# Revit family: RS500.80.x.245
name_source: partatom
category: Allgemeines Modell
units: mm (PartAtom-declared; Revit-internal decimal feet)

## family parameters
Arbeitsebenenbasiert = Nein
Beim Laden mit Abzugskörper schneiden = Nein
Bemaßung runder Anschluss = Durchmesser verwenden
Gemeinsam genutzt = Nein
Immer vertikal = Ja
Kann Basisbauteil für Bewehrung sein = Nein
Raumberechnungspunkt = Nein
Teiletyp = Normal

## types (1)
- DN80
    Anschlusswert DU L/s = 0
    Baugruppenkennzeichen = D2030300
    Hersteller = Resitec
    RS_AVol-H = 200 mm  [stored 0.656168 ft]
    RS_AVol-L = 129 mm  [stored 0.423228 ft]
    RS_AVol-T = 129 mm  [stored 0.423228 ft]
    RS_DN1 = 80 mm  [stored 0.262467 ft]
    RS_DN1d = 88 mm  [stored 0.288714 ft]
    RS_DN2 = 180 mm  [stored 0.590551 ft]
    RS_DVol-L = 200 mm  [stored 0.656168 ft]
    RS_DVol-T = 200 mm  [stored 0.656168 ft]
    RS_Klbl = 2 mm  [stored 0.00656168 ft]
    RS_Manufacture = Resitec
    RS_URL = https://resitec.ch
    RS_dia001 = 245 mm  [stored 0.803806 ft]
    RS_dia002 = 130 mm  [stored 0.426509 ft]
    RS_dim001 = 23 mm  [stored 0.0754593 ft]
    RS_dim002 = 30 mm  [stored 0.0984252 ft]
    RS_dim003 = 22 mm
    RS_s = 1 mm  [stored 0.00328084 ft]
    RS_s001 = 3 mm  [stored 0.00984252 ft]
    URL = https://www.resitec.ch
    Vorgabe-Ansicht = 0 mm  [stored 0 ft]

note: [stored X ft] marks values corroborated as IEEE doubles in the binary element streams (Revit-internal decimal feet)

## geometry (parser evidence)
native form markers: Blend x8
no freeform markers — native parametric forms only
